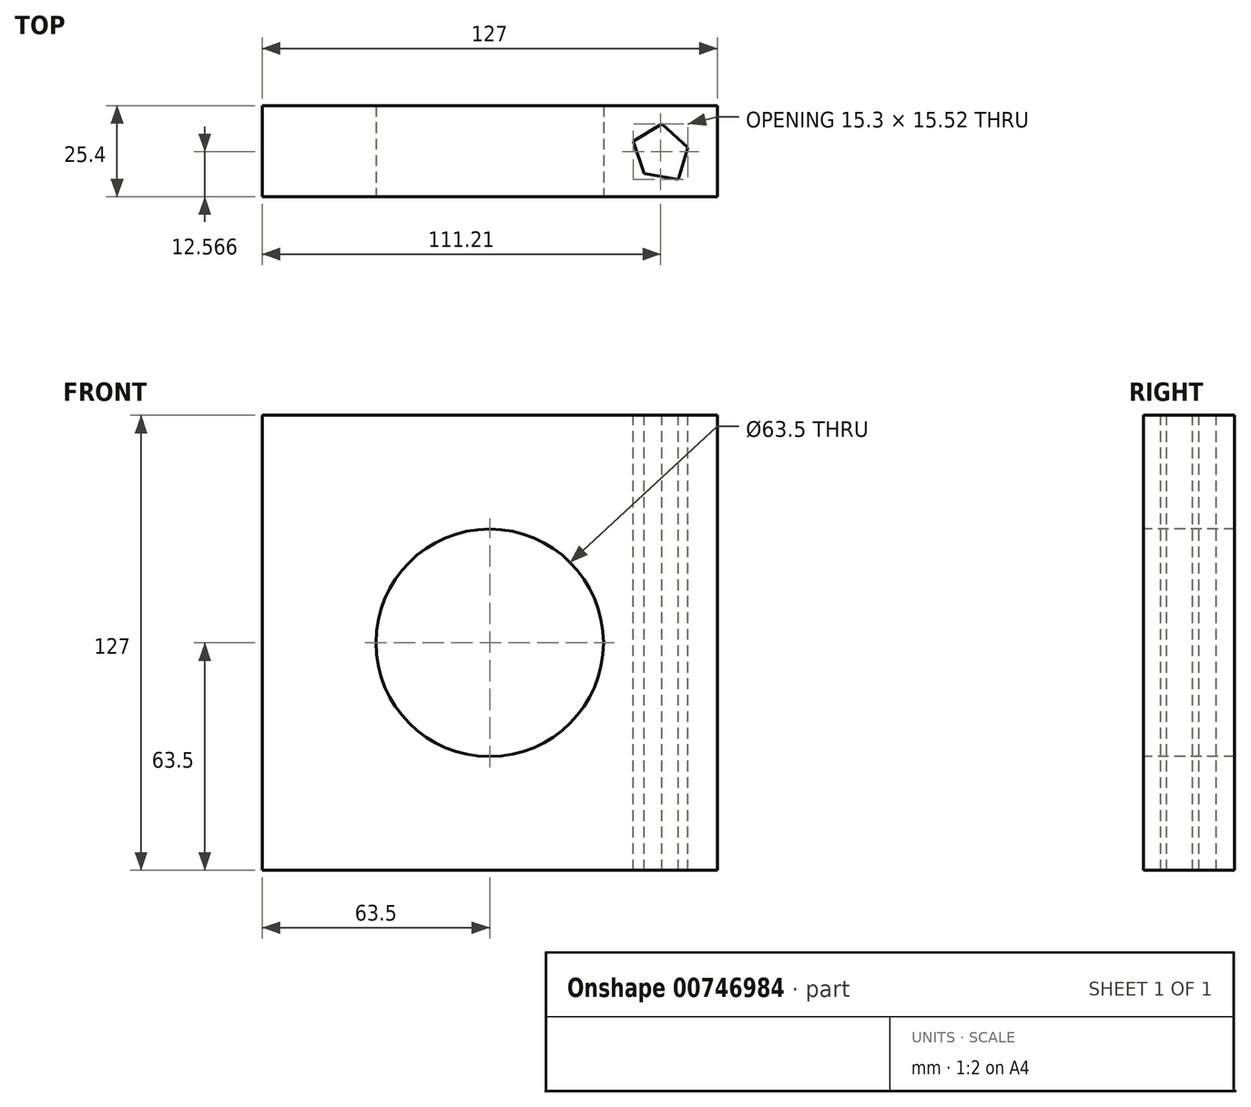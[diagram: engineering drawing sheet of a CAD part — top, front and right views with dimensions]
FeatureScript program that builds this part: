
annotation { "Feature Type Name" : "Feature", "Feature Type Description" : "" }
export const myFeature = defineFeature(function(context is Context, id is Id, definition is map)
    precondition{}
    {
        {
            var Q0;
            Q0=qCreatedBy(makeId("Front.planeOp"),FACE);
            var sketch = newSketch(context, id + "F0", { "sketchPlane" : qUnion([Q0])});
            skLineSegment(sketch, "E0.bottom", {"start": v(0, 0) * mm, "end": v(127, 0) * mm});
            skLineSegment(sketch, "E0.top", {"start": v(0, 127) * mm, "end": v(127, 127) * mm});
            skLineSegment(sketch, "E0.left", {"start": v(0, 0) * mm, "end": v(0, 127) * mm});
            skLineSegment(sketch, "E0.right", {"start": v(127, 0) * mm, "end": v(127, 127) * mm});
            skSolve(sketch);
        }
        {
            var Q0;
            Q0=makeQuery(id+"F0.imprint","IMPRINT",FACE,{"disambiguationData":[TD([[makeQuery(id+"F0.imprint","IMPRINT",EDGE,{"derivedFrom":sQuery(id+"F0.wireOp",EDGE,"E0.bottom")}),1.0]])]});
            extrude(context, id + "F1", {"entities" : qUnion([Q0]), "depth" : 25.4 * mm, "offsetDistance" : 25.4 * mm});
        }
        {
            var Q0;
            Q0=makeQuery(id+"F1.opExtrude","CAP_FACE",FACE,{"disambiguationData":[OSD([sQuery(id+"F0.wireOp",EDGE,"E0.bottom"),sQuery(id+"F0.wireOp",EDGE,"E0.top"),sQuery(id+"F0.wireOp",EDGE,"E0.left"),sQuery(id+"F0.wireOp",EDGE,"E0.right")])],"isStart":false});
            var sketch = newSketch(context, id + "F2", { "sketchPlane" : qUnion([Q0])});
            skPoint(sketch, "E1.centerSnap0", {"position": v(0, 63.5) * mm});
            skCircle(sketch, "E2", {"center": v(63.5, 63.5) * mm, "radius": 31.75 * mm});
            skSolve(sketch);
        }
        {
            var Q0;
            Q0=makeQuery(id+"F2.imprint","IMPRINT",FACE,{"disambiguationData":[TD([[makeQuery(id+"F2.imprint","IMPRINT",EDGE,{"derivedFrom":sQuery(id+"F2.wireOp",EDGE,"E2")}),1.0]])]});
            extrude(context, id + "F3", {"entities" : qUnion([Q0]), "operationType" : NewBodyOperationType.REMOVE, "endBound" : BoundingType.THROUGH_ALL, "oppositeDirection" : true, "depth" : 25.4 * mm, "offsetDistance" : 25.4 * mm});
        }
        {
            var Q0;
            Q0=makeQuery(id+"F1.opExtrude","SWEPT_FACE",FACE,{"disambiguationData":[OSD([sQuery(id+"F0.wireOp",EDGE,"E0.top")])]});
            var sketch = newSketch(context, id + "F4", { "sketchPlane" : qUnion([Q0])});
            skLineSegment(sketch, "E3", {"start": v(103.56, -9.88) * mm, "end": v(111.6, -5.08) * mm});
            skLineSegment(sketch, "E4", {"start": v(111.6, -5.08) * mm, "end": v(118.86, -11.66) * mm});
            skLineSegment(sketch, "E5", {"start": v(118.86, -11.66) * mm, "end": v(116.18, -20.6) * mm});
            skLineSegment(sketch, "E6", {"start": v(116.18, -20.6) * mm, "end": v(106.58, -18.92) * mm});
            skLineSegment(sketch, "E7", {"start": v(106.58, -18.92) * mm, "end": v(103.56, -9.88) * mm});
            skSolve(sketch);
        }
        {
            var Q0;
            Q0=makeQuery(id+"F4.imprint","IMPRINT",FACE,{"disambiguationData":[TD([[makeQuery(id+"F4.imprint","IMPRINT",EDGE,{"derivedFrom":sQuery(id+"F4.wireOp",EDGE,"E3")}),-1.0]])]});
            extrude(context, id + "F5", {"entities" : qUnion([Q0]), "operationType" : NewBodyOperationType.REMOVE, "endBound" : BoundingType.THROUGH_ALL, "oppositeDirection" : true, "depth" : 19.05 * mm, "offsetDistance" : 25.4 * mm});
        }
    });
